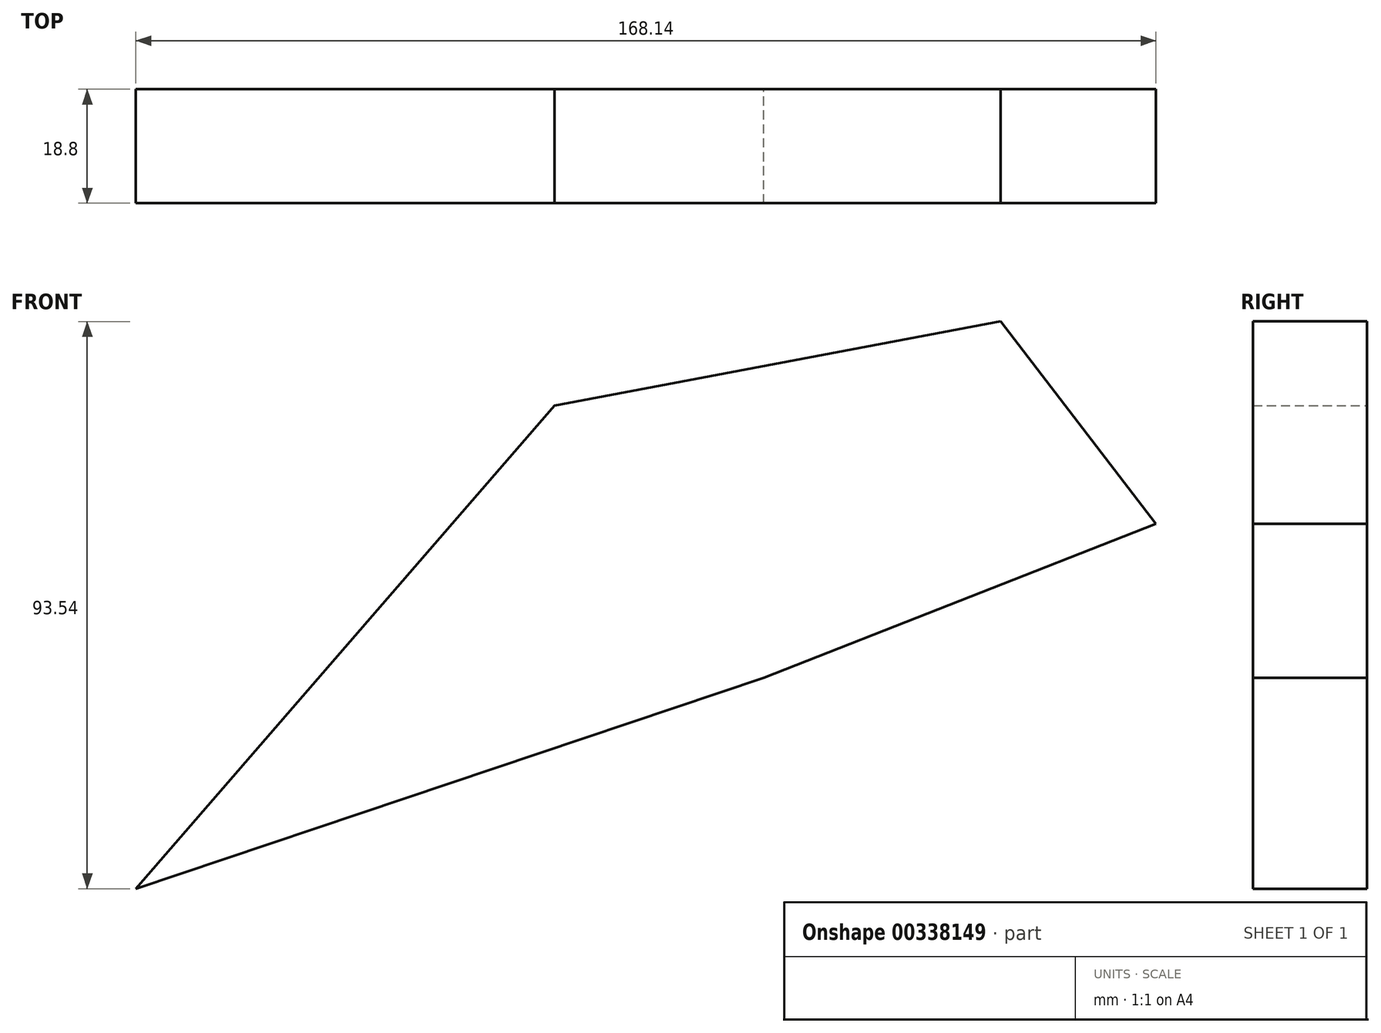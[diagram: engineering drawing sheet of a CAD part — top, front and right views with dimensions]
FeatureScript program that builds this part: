
annotation { "Feature Type Name" : "Feature", "Feature Type Description" : "" }
export const myFeature = defineFeature(function(context is Context, id is Id, definition is map)
    precondition{}
    {
        {
            var Q0;
            Q0=qCreatedBy(makeId("Front.planeOp"),FACE);
            var sketch = newSketch(context, id + "F0", { "sketchPlane" : qUnion([Q0])});
            skLineSegment(sketch, "E0", {"start": v(0, 0) * mm, "end": v(-44.55, 58.08) * mm});
            skLineSegment(sketch, "E1", {"start": v(0, 0) * mm, "end": v(-103.48, -34.78) * mm});
            skLineSegment(sketch, "E2", {"start": v(-103.48, -34.78) * mm, "end": v(-34.45, 44.92) * mm});
            skLineSegment(sketch, "E3", {"start": v(-34.45, 44.92) * mm, "end": v(39.06, 58.76) * mm});
            skLineSegment(sketch, "E4", {"start": v(39.06, 58.76) * mm, "end": v(64.66, 25.4) * mm});
            skLineSegment(sketch, "E5", {"start": v(64.66, 25.4) * mm, "end": v(0, 0) * mm});
            skSolve(sketch);
        }
        {
            var Q0;
            {var subQ2=sQuery(id+"F0.wireOp",EDGE,"E3");Q0=makeQuery(id+"F0.imprint","IMPRINT",FACE,{"disambiguationData":[TD([[makeQuery(id+"F0.imprint","IMPRINT",EDGE,{"derivedFrom":subQ2}),-1.0]])]});}
            var Q1;
            {var subQ0=sQuery(id+"F0.wireOp",EDGE,"E1");Q1=makeQuery(id+"F0.imprint","IMPRINT",FACE,{"disambiguationData":[TD([[makeQuery(id+"F0.imprint","IMPRINT",EDGE,{"derivedFrom":subQ0}),-1.0]])]});}
            extrude(context, id + "F1", {"entities" : qUnion([Q0, Q1]), "depth" : 18.8 * mm});
        }
        {
            var Q0;
            Q0=makeQuery(id+"F1.opExtrude","SWEPT_FACE",FACE,{"disambiguationData":[OSD([sQuery(id+"F0.wireOp",EDGE,"E4")])]});
            var sketch = newSketch(context, id + "F2", { "sketchPlane" : qUnion([Q0])});
            skLineSegment(sketch, "E6", {"start": v(-9.4, 22.85) * mm, "end": v(8.96, -76.63) * mm});
            skSolve(sketch);
        }
        {
            var Q0;
            Q0=sQuery(id+"F2.wireOp",EDGE,"E6");
            extrude(context, id + "F3", {"bodyType" : ToolBodyType.SURFACE, "surfaceEntities" : qUnion([Q0]), "depth" : 25.4 * mm});
        }
    });
